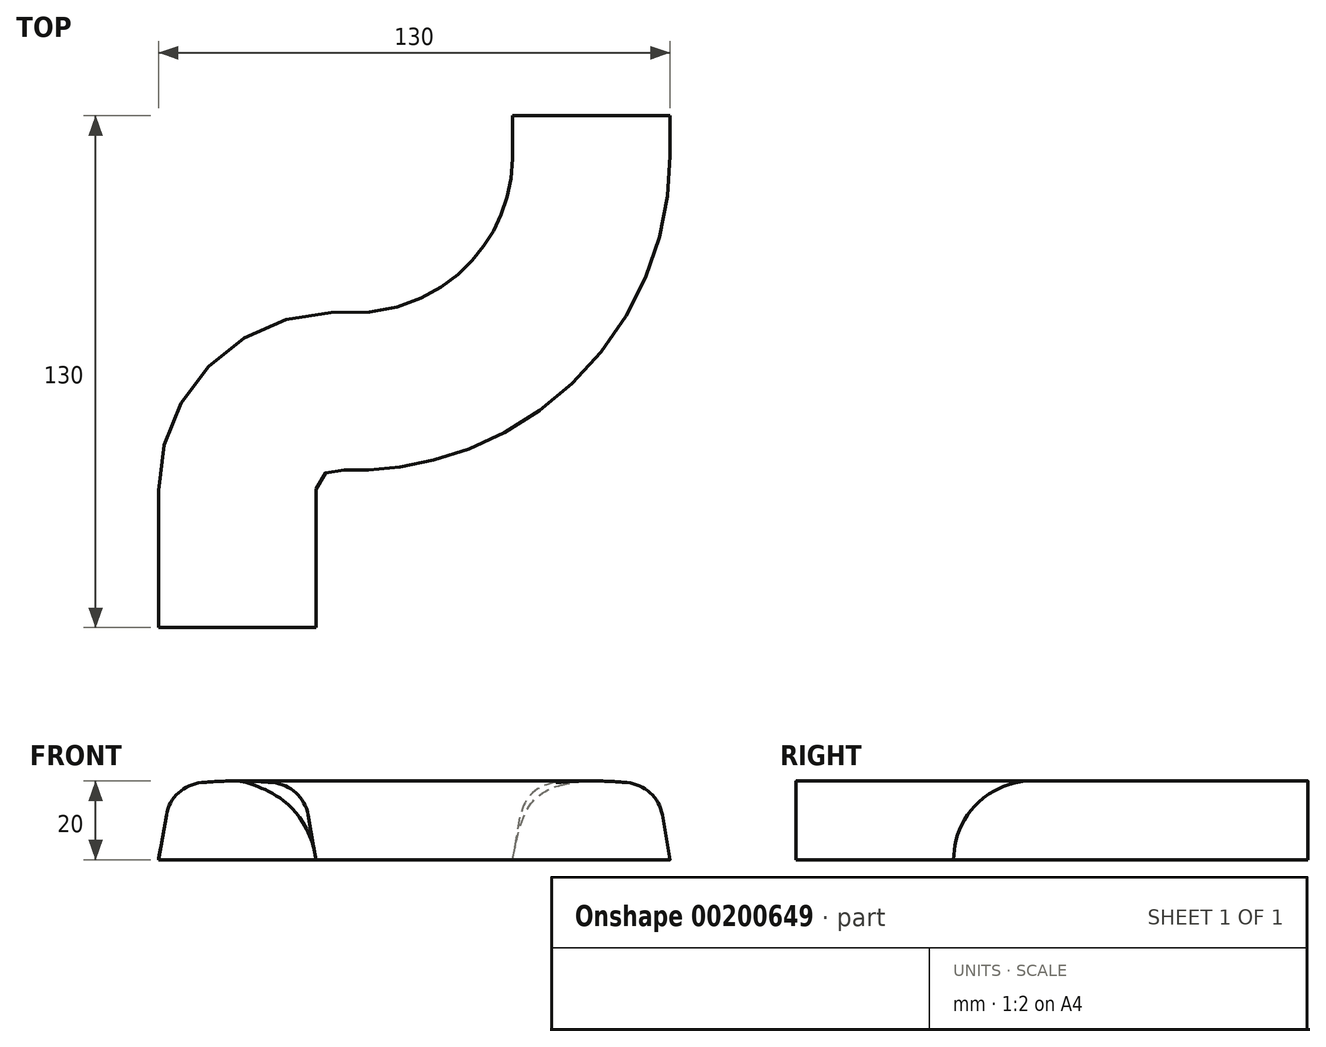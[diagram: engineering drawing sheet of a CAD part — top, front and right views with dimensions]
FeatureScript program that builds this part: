
annotation { "Feature Type Name" : "Feature", "Feature Type Description" : "" }
export const myFeature = defineFeature(function(context is Context, id is Id, definition is map)
    precondition{}
    {
        {
            var Q0;
            Q0=qCreatedBy(makeId("Top.planeOp"),FACE);
            var sketch = newSketch(context, id + "F0", { "sketchPlane" : qUnion([Q0])});
            skLineSegment(sketch, "E0", {"start": v(-30, -60) * mm, "end": v(-30, -25) * mm});
            skLineSegment(sketch, "E1", {"start": v(-5, 0) * mm, "end": v(0, 0) * mm});
            skLineSegment(sketch, "E2", {"start": v(60, 60) * mm, "end": v(60, 70) * mm});
            skPoint(sketch, "E3.visualSharp", {"position": v(-30, 0) * mm});
            skArc(sketch, "E3.filletArc", {"start": v(-5, 0) * mm, "mid": v(-22.68, -7.32) * mm, "end": v(-30, -25) * mm});
            skPoint(sketch, "E4.visualSharp", {"position": v(60, 0) * mm});
            skArc(sketch, "E4.filletArc", {"start": v(0, 0) * mm, "mid": v(42.43, 17.57) * mm, "end": v(60, 60) * mm});
            skSolve(sketch);
        }
        {
            var Q0;
            Q0=sQuery(id+"F0.wireOp",EDGE,"E0");
            var Q1;
            Q1=sQuery(id+"F0.wireOp",VERTEX,"E0.start");
            cPlane(context, id + "F1", {"entities" : qUnion([Q0, Q1]), "cplaneType" : CPlaneType.CURVE_POINT, "offset" : 25 * mm, "width" : 150 * mm, "height" : 150 * mm});
        }
        {
            var Q0;
            Q0=qCreatedBy(id+"F1.planeOp",FACE);
            var sketch = newSketch(context, id + "F2", { "sketchPlane" : qUnion([Q0])});
            skLineSegment(sketch, "E5.bottom", {"start": v(10, -20) * mm, "end": v(50, -20) * mm, "construction": true});
            skLineSegment(sketch, "E5.top", {"start": v(10, 0) * mm, "end": v(50, 0) * mm, "construction": true});
            skLineSegment(sketch, "E5.left", {"start": v(10, -20) * mm, "end": v(10, 0) * mm, "construction": true});
            skLineSegment(sketch, "E5.right", {"start": v(50, -20) * mm, "end": v(50, 0) * mm, "construction": true});
            skPoint(sketch, "E5.middle", {"position": v(30, -10) * mm});
            skLineSegment(sketch, "E6", {"start": v(30, 0) * mm, "end": v(30, -20) * mm, "construction": true});
            skLineSegment(sketch, "E7", {"start": v(50, -20) * mm, "end": v(48, -8.63) * mm});
            skLineSegment(sketch, "E8.MirrorCS", {"start": v(10, -20) * mm, "end": v(12, -8.63) * mm});
            skArc(sketch, "E9", {"start": v(39.05, -0.41) * mm, "mid": v(30, 0) * mm, "end": v(20.95, -0.41) * mm});
            skPoint(sketch, "E10.visualSharp", {"position": v(46.72, -1.4) * mm});
            skArc(sketch, "E10.filletArc", {"start": v(48, -8.63) * mm, "mid": v(44.92, -3) * mm, "end": v(39.05, -0.41) * mm});
            skPoint(sketch, "E11.visualSharp", {"position": v(13.28, -1.4) * mm});
            skArc(sketch, "E11.filletArc", {"start": v(20.95, -0.41) * mm, "mid": v(15.08, -3) * mm, "end": v(12, -8.63) * mm});
            skSolve(sketch);
        }
        {
            var Q0;
            Q0=qCreatedBy(makeId("Right.planeOp"),FACE);
            var sketch = newSketch(context, id + "F3", { "sketchPlane" : qUnion([Q0])});
            skLineSegment(sketch, "E12.bottom", {"start": v(-20, -20) * mm, "end": v(20, -20) * mm, "construction": true});
            skLineSegment(sketch, "E12.top", {"start": v(-20, 0) * mm, "end": v(20, 0) * mm, "construction": true});
            skLineSegment(sketch, "E12.left", {"start": v(-20, -20) * mm, "end": v(-20, 0) * mm, "construction": true});
            skLineSegment(sketch, "E12.right", {"start": v(20, -20) * mm, "end": v(20, 0) * mm, "construction": true});
            skPoint(sketch, "E12.middle", {"position": v(0, -10) * mm});
            skLineSegment(sketch, "E13", {"start": v(0, 0) * mm, "end": v(0, -20) * mm, "construction": true});
            skArc(sketch, "E14", {"start": v(20, -20) * mm, "mid": v(0, 0) * mm, "end": v(-20, -20) * mm});
            skSolve(sketch);
        }
        {
            var Q0;
            Q0=sQuery(id+"F0.wireOp",EDGE,"E2");
            var Q1;
            Q1=sQuery(id+"F0.wireOp",VERTEX,"E2.end");
            cPlane(context, id + "F4", {"entities" : qUnion([Q0, Q1]), "cplaneType" : CPlaneType.CURVE_POINT, "offset" : 25 * mm, "width" : 150 * mm, "height" : 150 * mm});
        }
        {
            var Q0;
            Q0=qCreatedBy(id+"F4.planeOp",FACE);
            var sketch = newSketch(context, id + "F5", { "sketchPlane" : qUnion([Q0])});
            skLineSegment(sketch, "E15.bottom", {"start": v(-80, -20) * mm, "end": v(-40, -20) * mm, "construction": true});
            skLineSegment(sketch, "E15.top", {"start": v(-80, 0) * mm, "end": v(-40, 0) * mm, "construction": true});
            skLineSegment(sketch, "E15.left", {"start": v(-80, -20) * mm, "end": v(-80, 0) * mm, "construction": true});
            skLineSegment(sketch, "E15.right", {"start": v(-40, -20) * mm, "end": v(-40, 0) * mm, "construction": true});
            skPoint(sketch, "E15.middle", {"position": v(-60, -10) * mm});
            skLineSegment(sketch, "E16", {"start": v(-60, 0) * mm, "end": v(-60, -20) * mm, "construction": true});
            skLineSegment(sketch, "E17", {"start": v(-40, -20) * mm, "end": v(-42, -8.63) * mm});
            skLineSegment(sketch, "E18.MirrorCS", {"start": v(-80, -20) * mm, "end": v(-78, -8.63) * mm});
            skArc(sketch, "E19", {"start": v(-50.95, -0.41) * mm, "mid": v(-60, 0) * mm, "end": v(-69.05, -0.41) * mm});
            skPoint(sketch, "E20.visualSharp", {"position": v(-43.28, -1.4) * mm});
            skArc(sketch, "E20.filletArc", {"start": v(-42, -8.63) * mm, "mid": v(-45.08, -3) * mm, "end": v(-50.95, -0.41) * mm});
            skPoint(sketch, "E21.visualSharp", {"position": v(-76.72, -1.4) * mm});
            skArc(sketch, "E21.filletArc", {"start": v(-69.05, -0.41) * mm, "mid": v(-74.92, -3) * mm, "end": v(-78, -8.63) * mm});
            skSolve(sketch);
        }
        {
            var Q0;
            Q0=qCreatedBy(makeId("Top.planeOp"),FACE);
            cPlane(context, id + "F6", {"entities" : qUnion([Q0]), "cplaneType" : CPlaneType.OFFSET, "offset" : 20 * mm, "oppositeDirection" : true, "width" : 150 * mm, "height" : 150 * mm});
        }
        {
            var Q0;
            Q0=qCreatedBy(id+"F6.planeOp",FACE);
            var sketch = newSketch(context, id + "F7", { "sketchPlane" : qUnion([Q0])});
            skLineSegment(sketch, "E22.0", {"start": v(80, 60) * mm, "end": v(80, 70) * mm});
            skLineSegment(sketch, "E22.1", {"start": v(-10, -60) * mm, "end": v(-10, -25) * mm});
            skArc(sketch, "E22.2", {"start": v(-5, -20) * mm, "mid": v(-8.54, -21.46) * mm, "end": v(-10, -25) * mm});
            skLineSegment(sketch, "E22.3", {"start": v(-5, -20) * mm, "end": v(0, -20) * mm});
            skArc(sketch, "E22.4", {"start": v(0, -20) * mm, "mid": v(56.57, 3.43) * mm, "end": v(80, 60) * mm});
            skSolve(sketch);
        }
        {
            var Q0;
            Q0=qCreatedBy(id+"F6.planeOp",FACE);
            var sketch = newSketch(context, id + "F8", { "sketchPlane" : qUnion([Q0])});
            skLineSegment(sketch, "E23.0", {"start": v(40, 60) * mm, "end": v(40, 70) * mm});
            skLineSegment(sketch, "E23.1", {"start": v(-50, -60) * mm, "end": v(-50, -25) * mm});
            skArc(sketch, "E23.2", {"start": v(-5, 20) * mm, "mid": v(-36.82, 6.82) * mm, "end": v(-50, -25) * mm});
            skLineSegment(sketch, "E23.3", {"start": v(-5, 20) * mm, "end": v(0, 20) * mm});
            skArc(sketch, "E23.4", {"start": v(0, 20) * mm, "mid": v(28.28, 31.72) * mm, "end": v(40, 60) * mm});
            skSolve(sketch);
        }
        {
            var Q0;
            Q0 = qConstructionFilter(qBodyType(qCreatedBy(id + "F2" ,EDGE), BodyType.WIRE), ConstructionObject.NO);
            var Q1;
            Q1 = qConstructionFilter(qBodyType(qCreatedBy(id + "F3" ,EDGE), BodyType.WIRE), ConstructionObject.NO);
            var Q2;
            Q2 = qConstructionFilter(qBodyType(qCreatedBy(id + "F5" ,EDGE), BodyType.WIRE), ConstructionObject.NO);
            var Q3;
            Q3 = qConstructionFilter(qBodyType(qCreatedBy(id + "F0" ,EDGE), BodyType.WIRE), ConstructionObject.NO);
            var Q4;
            Q4 = qConstructionFilter(qBodyType(qCreatedBy(id + "F7" ,EDGE), BodyType.WIRE), ConstructionObject.NO);
            var Q5;
            Q5 = qConstructionFilter(qBodyType(qCreatedBy(id + "F8" ,EDGE), BodyType.WIRE), ConstructionObject.NO);
            loft(context, id + "F9", {"bodyType" : ToolBodyType.SURFACE, "addGuides" : true, "wireProfilesArray" : [{ "wireProfileEntities" : qUnion([Q0]) }, { "wireProfileEntities" : qUnion([Q1]) }, { "wireProfileEntities" : qUnion([Q2]) }], "guidesArray" : [{ "guideEntities" : qUnion([Q3]), "guideDerivativeType" : LoftGuideDerivativeType.DEFAULT, "guideDerivativeMagnitude" : 1 }, { "guideEntities" : qUnion([Q4]), "guideDerivativeType" : LoftGuideDerivativeType.DEFAULT, "guideDerivativeMagnitude" : 1 }, { "guideEntities" : qUnion([Q5]), "guideDerivativeType" : LoftGuideDerivativeType.DEFAULT, "guideDerivativeMagnitude" : 1 }]});
        }
    });
